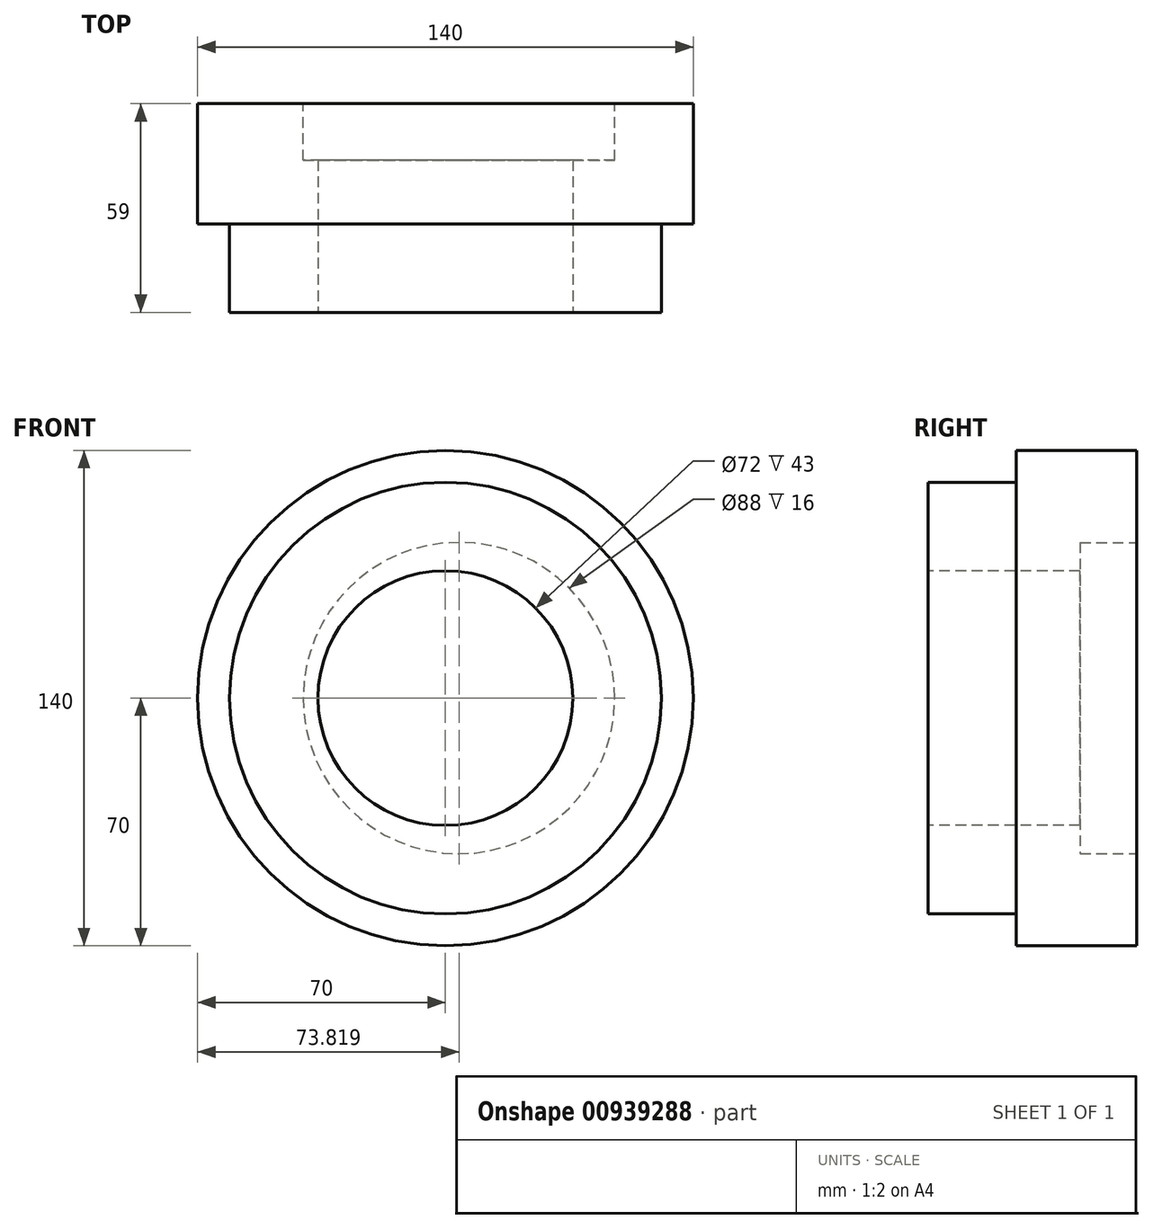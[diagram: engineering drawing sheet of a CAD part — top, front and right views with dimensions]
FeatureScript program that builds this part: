
annotation { "Feature Type Name" : "Feature", "Feature Type Description" : "" }
export const myFeature = defineFeature(function(context is Context, id is Id, definition is map)
    precondition{}
    {
        {
            var Q0;
            Q0=qCreatedBy(makeId("Front.planeOp"),FACE);
            var sketch = newSketch(context, id + "F0", { "sketchPlane" : qUnion([Q0])});
            skCircle(sketch, "E0", {"center": v(0, 0) * mm, "radius": 70 * mm});
            skSolve(sketch);
        }
        {
            var Q0;
            Q0=makeQuery(id+"F0.imprint","IMPRINT",FACE,{"disambiguationData":[TD([[makeQuery(id+"F0.imprint","IMPRINT",EDGE,{"derivedFrom":sQuery(id+"F0.wireOp",EDGE,"E0")}),1.0]])]});
            extrude(context, id + "F1", {"entities" : qUnion([Q0]), "oppositeDirection" : true, "depth" : 59 * mm, "offsetDistance" : 25 * mm});
        }
        {
            var Q0;
            Q0=makeQuery(id+"F1.opExtrude","CAP_FACE",FACE,{"disambiguationData":[OSD([sQuery(id+"F0.wireOp",EDGE,"E0")])],"isStart":true});
            var sketch = newSketch(context, id + "F2", { "sketchPlane" : qUnion([Q0])});
            skCircle(sketch, "E1", {"center": v(0, 0) * mm, "radius": 61 * mm});
            skSolve(sketch);
        }
        {
            var Q0;
            Q0=makeQuery(id+"F2.imprint","IMPRINT",FACE,{"disambiguationData":[TD([[makeQuery(id+"F2.imprint","IMPRINT",EDGE,{"derivedFrom":sQuery(id+"F2.wireOp",EDGE,"E1")}),-1.0]])]});
            extrude(context, id + "F3", {"entities" : qUnion([Q0]), "operationType" : NewBodyOperationType.REMOVE, "oppositeDirection" : true, "depth" : 25 * mm, "offsetDistance" : 25 * mm});
        }
        {
            var Q0;
            Q0=makeQuery(id+"F1.opExtrude","CAP_FACE",FACE,{"disambiguationData":[OSD([sQuery(id+"F0.wireOp",EDGE,"E0")])],"isStart":true});
            var sketch = newSketch(context, id + "F4", { "sketchPlane" : qUnion([Q0])});
            skCircle(sketch, "E2", {"center": v(0, 0) * mm, "radius": 36 * mm});
            skSolve(sketch);
        }
        {
            var Q0;
            Q0=makeQuery(id+"F4.imprint","IMPRINT",FACE,{"disambiguationData":[TD([[makeQuery(id+"F4.imprint","IMPRINT",EDGE,{"derivedFrom":sQuery(id+"F4.wireOp",EDGE,"E2")}),1.0]])]});
            extrude(context, id + "F5", {"entities" : qUnion([Q0]), "operationType" : NewBodyOperationType.REMOVE, "endBound" : BoundingType.UP_TO_NEXT, "oppositeDirection" : true, "depth" : 25 * mm, "offsetDistance" : 25 * mm});
        }
        {
            var Q0;
            Q0=makeQuery(id+"F1.opExtrude","CAP_FACE",FACE,{"disambiguationData":[OSD([sQuery(id+"F0.wireOp",EDGE,"E0")])],"isStart":false});
            var sketch = newSketch(context, id + "F6", { "sketchPlane" : qUnion([Q0])});
            skCircle(sketch, "E3", {"center": v(-3.82, 0) * mm, "radius": 44 * mm});
            skSolve(sketch);
        }
        {
            var Q0;
            Q0=makeQuery(id+"F6.imprint","IMPRINT",FACE,{"disambiguationData":[TD([[makeQuery(id+"F6.imprint","IMPRINT",EDGE,{"derivedFrom":sQuery(id+"F6.wireOp",EDGE,"E3")}),1.0]])]});
            extrude(context, id + "F7", {"entities" : qUnion([Q0]), "operationType" : NewBodyOperationType.REMOVE, "oppositeDirection" : true, "depth" : 16 * mm, "offsetDistance" : 25 * mm});
        }
    });
